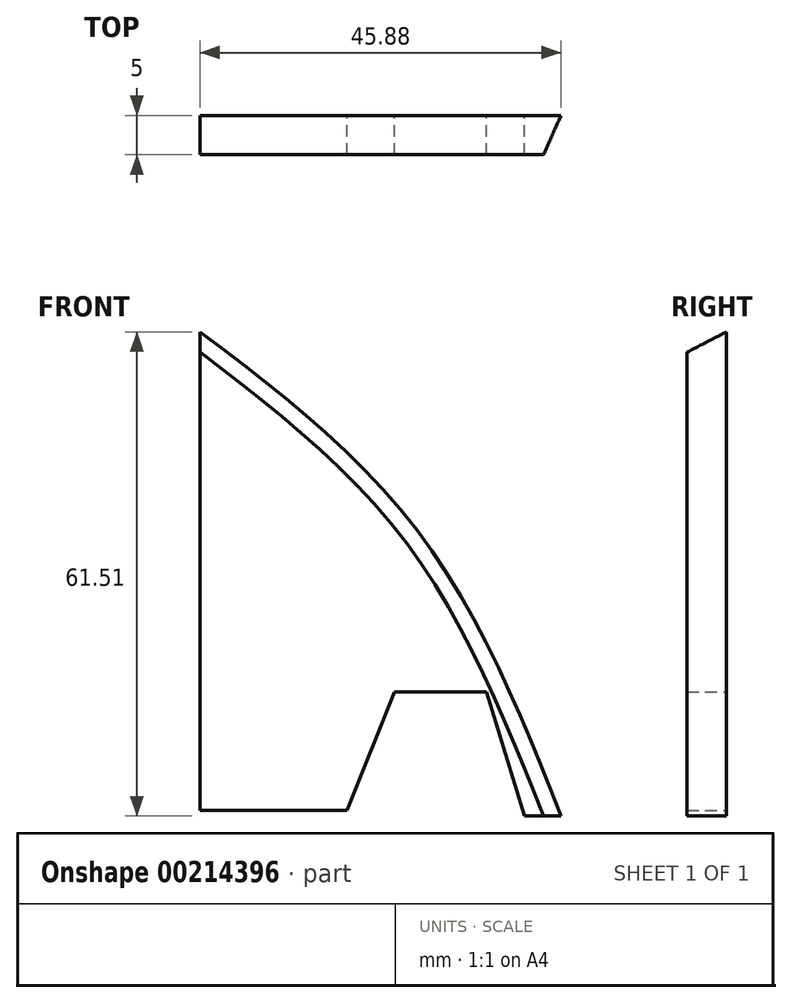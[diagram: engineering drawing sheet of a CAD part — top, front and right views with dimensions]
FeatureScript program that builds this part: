
annotation { "Feature Type Name" : "Feature", "Feature Type Description" : "" }
export const myFeature = defineFeature(function(context is Context, id is Id, definition is map)
    precondition{}
    {
        {
            var Q0;
            Q0=qCreatedBy(makeId("Front.planeOp"),FACE);
            var sketch = newSketch(context, id + "F0", { "sketchPlane" : qUnion([Q0])});
            skFitSpline(sketch, "E0", {"points": [v(0, 58.5) * mm, v(35.51, 27.15) * mm, v(56.9, -15.75) * mm], "startDerivative": vector(78.36, -57.25) * mm, "endDerivative": vector(35.5, -91.23) * mm});
            skLineSegment(sketch, "E1", {"start": v(56.9, -15.75) * mm, "end": v(41.26, -15.75) * mm});
            skLineSegment(sketch, "E2", {"start": v(41.26, -15.75) * mm, "end": v(36.44, 0) * mm});
            skLineSegment(sketch, "E3", {"start": v(36.44, 0) * mm, "end": v(24.71, 0) * mm});
            skLineSegment(sketch, "E4", {"start": v(24.71, 0) * mm, "end": v(18.7, -15.01) * mm});
            skLineSegment(sketch, "E5", {"start": v(18.7, -15.01) * mm, "end": v(0, -15.01) * mm});
            skLineSegment(sketch, "E6", {"start": v(0, -15.01) * mm, "end": v(0, 58.5) * mm});
            skSolve(sketch);
        }
        {
            var Q0;
            Q0 = qSketchRegion(id + "F0", true);
            extrude(context, id + "F1", {"entities" : qUnion([Q0]), "depth" : 5 * mm});
        }
        {
            var Q0;
            Q0=makeQuery(id+"F1.opExtrude","CAP_EDGE",EDGE,{"disambiguationData":[OSD([sQuery(id+"F0.wireOp",EDGE,"E0")])],"isStart":true});
            chamfer(context, id + "F2", {"entities" : qUnion([Q0]), "width" : 5.08 * mm, "tangentPropagation" : true});
        }
        {
            var Q0;
            {var subQ0=sQuery(id+"F0.wireOp",EDGE,"E0");Q0=makeQuery(id+"F2.opChamfer","BLEND_EDGE",EDGE,{"blendedFrom":[makeQuery(id+"F1.opExtrude","CAP_EDGE",EDGE,{"disambiguationData":[OSD([subQ0])],"isStart":true}),makeQuery(id+"F1.opExtrude","CAP_FACE",FACE,{"disambiguationData":[OSD([subQ0,sQuery(id+"F0.wireOp",EDGE,"E1"),sQuery(id+"F0.wireOp",EDGE,"E2"),sQuery(id+"F0.wireOp",EDGE,"E3"),sQuery(id+"F0.wireOp",EDGE,"E4"),sQuery(id+"F0.wireOp",EDGE,"E5"),sQuery(id+"F0.wireOp",EDGE,"E6")])],"isStart":false})],"blendedInto":[makeQuery(id+"F1.opExtrude","CAP_FACE",FACE,{"disambiguationData":[OSD([subQ0,sQuery(id+"F0.wireOp",EDGE,"E1"),sQuery(id+"F0.wireOp",EDGE,"E2"),sQuery(id+"F0.wireOp",EDGE,"E3"),sQuery(id+"F0.wireOp",EDGE,"E4"),sQuery(id+"F0.wireOp",EDGE,"E5"),sQuery(id+"F0.wireOp",EDGE,"E6")])],"isStart":false})]});}
            chamfer(context, id + "F3", {"entities" : qUnion([Q0]), "width" : 5.08 * mm, "tangentPropagation" : true});
        }
    });
